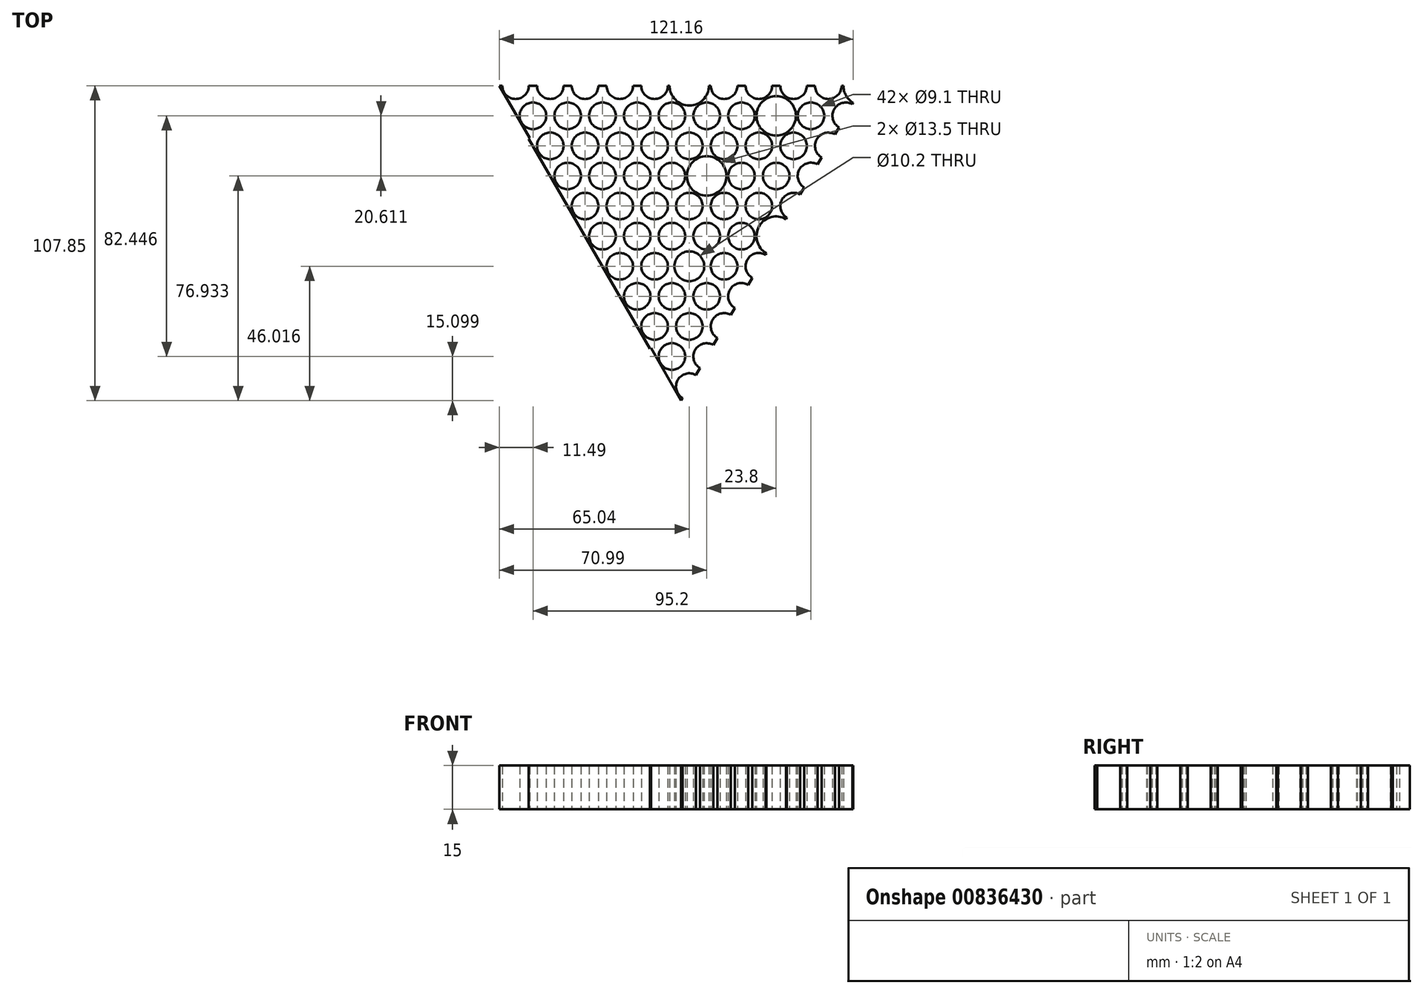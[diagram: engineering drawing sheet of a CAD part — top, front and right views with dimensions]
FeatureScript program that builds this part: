
annotation { "Feature Type Name" : "Feature", "Feature Type Description" : "" }
export const myFeature = defineFeature(function(context is Context, id is Id, definition is map)
    precondition{}
    {
        {
            var Q0;
            Q0=qCreatedBy(makeId("Top.planeOp"),FACE);
            var sketch = newSketch(context, id + "F0", { "sketchPlane" : qUnion([Q0])});
            skLineSegment(sketch, "E0.2", {"start": v(-62.5, -108.25) * mm, "end": v(-125, 0) * mm});
            skCircle(sketch, "E1", {"center": v(0, 0) * mm, "radius": 6.75 * mm});
            skCircle(sketch, "E2", {"center": v(-11.9, 0) * mm, "radius": 4.55 * mm});
            skCircle(sketch, "E3", {"center": v(-5.95, -10.3) * mm, "radius": 4.55 * mm});
            skCircle(sketch, "E4", {"center": v(-119, 0) * mm, "radius": 4.55 * mm});
            skCircle(sketch, "E5", {"center": v(-59.5, -103.06) * mm, "radius": 4.55 * mm});
            skCircle(sketch, "E6", {"center": v(-113.05, -10.3) * mm, "radius": 4.55 * mm});
            skCircle(sketch, "E7", {"center": v(-107.1, -20.61) * mm, "radius": 4.55 * mm});
            skCircle(sketch, "E8", {"center": v(-101.15, -30.92) * mm, "radius": 4.55 * mm});
            skCircle(sketch, "E9", {"center": v(-95.2, -41.22) * mm, "radius": 4.55 * mm});
            skCircle(sketch, "E10", {"center": v(-89.25, -51.53) * mm, "radius": 4.55 * mm});
            skCircle(sketch, "E11", {"center": v(-83.3, -61.83) * mm, "radius": 4.55 * mm});
            skCircle(sketch, "E12", {"center": v(-77.35, -72.14) * mm, "radius": 4.55 * mm});
            skCircle(sketch, "E13", {"center": v(-71.4, -82.45) * mm, "radius": 4.55 * mm});
            skCircle(sketch, "E14", {"center": v(-65.45, -92.75) * mm, "radius": 4.55 * mm});
            skLineSegment(sketch, "E15", {"start": v(-125, 0) * mm, "end": v(0, 0) * mm});
            skLineSegment(sketch, "E16", {"start": v(-62.5, -108.25) * mm, "end": v(0, 0) * mm});
            skCircle(sketch, "E17", {"center": v(-53.55, -92.75) * mm, "radius": 4.55 * mm});
            skCircle(sketch, "E18", {"center": v(-47.6, -82.45) * mm, "radius": 4.55 * mm});
            skCircle(sketch, "E19", {"center": v(-41.65, -72.14) * mm, "radius": 4.55 * mm});
            skCircle(sketch, "E20", {"center": v(-35.7, -61.83) * mm, "radius": 4.55 * mm});
            skCircle(sketch, "E21", {"center": v(-29.75, -51.53) * mm, "radius": 6.75 * mm});
            skCircle(sketch, "E22", {"center": v(-23.8, -41.22) * mm, "radius": 4.55 * mm});
            skCircle(sketch, "E23", {"center": v(-17.85, -30.92) * mm, "radius": 4.55 * mm});
            skCircle(sketch, "E24", {"center": v(-11.9, -20.61) * mm, "radius": 4.55 * mm});
            skCircle(sketch, "E25", {"center": v(-59.5, -82.45) * mm, "radius": 4.55 * mm});
            skCircle(sketch, "E26", {"center": v(-53.55, -72.14) * mm, "radius": 4.55 * mm});
            skCircle(sketch, "E27", {"center": v(-47.6, -61.83) * mm, "radius": 4.55 * mm});
            skCircle(sketch, "E28", {"center": v(-41.65, -51.53) * mm, "radius": 4.55 * mm});
            skCircle(sketch, "E29", {"center": v(-35.7, -41.22) * mm, "radius": 4.55 * mm});
            skCircle(sketch, "E30", {"center": v(-29.75, -30.92) * mm, "radius": 4.55 * mm});
            skCircle(sketch, "E31", {"center": v(-23.8, -20.61) * mm, "radius": 4.55 * mm});
            skCircle(sketch, "E32", {"center": v(-17.85, -10.3) * mm, "radius": 4.55 * mm});
            skCircle(sketch, "E33", {"center": v(-107.1, 0) * mm, "radius": 4.55 * mm});
            skCircle(sketch, "E34", {"center": v(-95.2, 0) * mm, "radius": 4.55 * mm});
            skCircle(sketch, "E35", {"center": v(-83.3, 0) * mm, "radius": 4.55 * mm});
            skCircle(sketch, "E36", {"center": v(-71.4, 0) * mm, "radius": 4.55 * mm});
            skCircle(sketch, "E37", {"center": v(-59.5, 0) * mm, "radius": 6.75 * mm});
            skCircle(sketch, "E38", {"center": v(-47.6, 0) * mm, "radius": 4.55 * mm});
            skCircle(sketch, "E39", {"center": v(-35.7, 0) * mm, "radius": 4.55 * mm});
            skCircle(sketch, "E40", {"center": v(-23.8, 0) * mm, "radius": 4.55 * mm});
            skCircle(sketch, "E41", {"center": v(-101.15, -10.3) * mm, "radius": 4.55 * mm});
            skCircle(sketch, "E42", {"center": v(-89.25, -10.3) * mm, "radius": 4.55 * mm});
            skCircle(sketch, "E43", {"center": v(-77.35, -10.3) * mm, "radius": 4.55 * mm});
            skCircle(sketch, "E44", {"center": v(-65.45, -10.3) * mm, "radius": 4.55 * mm});
            skCircle(sketch, "E45", {"center": v(-53.55, -10.3) * mm, "radius": 4.55 * mm});
            skCircle(sketch, "E46", {"center": v(-41.65, -10.3) * mm, "radius": 4.55 * mm});
            skCircle(sketch, "E47", {"center": v(-29.75, -10.3) * mm, "radius": 6.75 * mm});
            skCircle(sketch, "E48", {"center": v(-95.2, -20.61) * mm, "radius": 4.55 * mm});
            skCircle(sketch, "E49", {"center": v(-89.25, -30.92) * mm, "radius": 4.55 * mm});
            skCircle(sketch, "E50", {"center": v(-83.3, -41.22) * mm, "radius": 4.55 * mm});
            skCircle(sketch, "E51", {"center": v(-77.35, -51.53) * mm, "radius": 4.55 * mm});
            skCircle(sketch, "E52", {"center": v(-65.45, -72.14) * mm, "radius": 4.55 * mm});
            skCircle(sketch, "E53", {"center": v(-71.4, -61.83) * mm, "radius": 4.55 * mm});
            skCircle(sketch, "E54", {"center": v(-83.3, -20.61) * mm, "radius": 4.55 * mm});
            skCircle(sketch, "E55", {"center": v(-35.7, -20.61) * mm, "radius": 4.55 * mm});
            skCircle(sketch, "E56", {"center": v(-59.5, -61.83) * mm, "radius": 5.1 * mm});
            skCircle(sketch, "E57", {"center": v(-77.35, -30.92) * mm, "radius": 4.55 * mm});
            skCircle(sketch, "E58", {"center": v(-71.4, -20.61) * mm, "radius": 4.55 * mm});
            skCircle(sketch, "E59", {"center": v(-59.5, -20.61) * mm, "radius": 4.55 * mm});
            skCircle(sketch, "E60", {"center": v(-47.6, -20.61) * mm, "radius": 4.55 * mm});
            skCircle(sketch, "E61", {"center": v(-65.45, -30.92) * mm, "radius": 4.55 * mm});
            skCircle(sketch, "E62", {"center": v(-53.55, -30.92) * mm, "radius": 6.75 * mm});
            skCircle(sketch, "E63", {"center": v(-41.65, -30.92) * mm, "radius": 4.55 * mm});
            skCircle(sketch, "E64", {"center": v(-71.4, -41.22) * mm, "radius": 4.55 * mm});
            skCircle(sketch, "E65", {"center": v(-59.5, -41.22) * mm, "radius": 4.55 * mm});
            skCircle(sketch, "E66", {"center": v(-47.6, -41.22) * mm, "radius": 4.55 * mm});
            skCircle(sketch, "E67", {"center": v(-53.55, -51.53) * mm, "radius": 4.55 * mm});
            skCircle(sketch, "E68", {"center": v(-65.45, -51.53) * mm, "radius": 4.55 * mm});
            skLineSegment(sketch, "E69", {"start": v(-73, -90.07) * mm, "end": v(-72.65, -89.87) * mm});
            skLineSegment(sketch, "E70", {"start": v(-72.65, -89.87) * mm, "end": v(-62.27, -107.85) * mm});
            skLineSegment(sketch, "E71", {"start": v(-114.5, -18.19) * mm, "end": v(-114.15, -17.99) * mm});
            skLineSegment(sketch, "E72", {"start": v(-114.15, -17.99) * mm, "end": v(-124.54, 0) * mm});
            skSolve(sketch);
        }
        {
            var Q0;
            Q0=makeQuery(id+"F0.imprint","IMPRINT",FACE,{"disambiguationData":[TD([[makeQuery(id+"F0.imprint","IMPRINT",EDGE,{"derivedFrom":sQuery(id+"F0.wireOp",EDGE,"E6")}),-1.0]])]});
            extrude(context, id + "F1", {"entities" : qUnion([Q0]), "depth" : 15 * mm, "offsetDistance" : 25 * mm});
        }
    });
